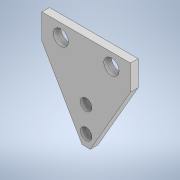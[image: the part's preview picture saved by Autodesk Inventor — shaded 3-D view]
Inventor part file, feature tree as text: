
AUTODESK INVENTOR PART (.ipt)
format: ipt  version: 2022 (Build 260153000, 153)  size: 132,608 bytes
history: native  units: mm
features: plane x7, extrude x1, mirror x1, sketch x1
ambient origin geometry x8: Origin, YZ Plane, XZ Plane, XY Plane, X Axis, Y Axis, Z Axis, Center Point
bodies: Solid1 (feature_tree)
feature tree (10):
  extrude  "Extrusion1"  Depth=10.0mm
  plane  "Work Plane4"
  mirror  "Mirror1"
  plane  "Work Plane10"
  plane  "Work Plane12"
  sketch  "Sketch1"  dims[d1=4.5mm d2=10.0mm d3=6.0mm d4=10.0mm d5=60.0deg d10=35.0mm d11=17.5mm d13=3.258248mm d17=120.0deg d18=3.0mm d19=0.0mm d20=10.0mm d22=23.0mm d25=-5.0mm d26=5.0mm]
  plane  "Work Plane1"
  plane  "Work Plane3"
  plane  "Work Plane5"
  plane  "Work Plane11"
